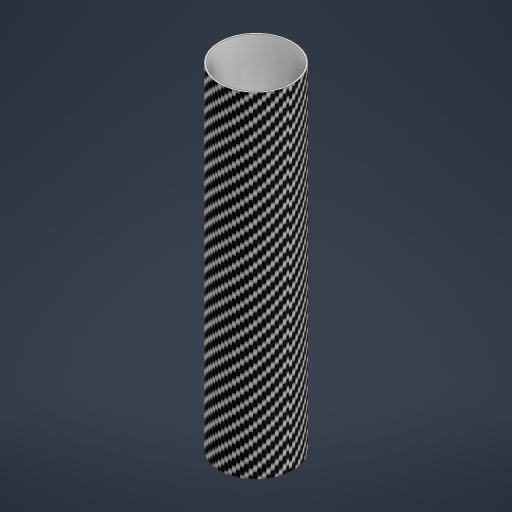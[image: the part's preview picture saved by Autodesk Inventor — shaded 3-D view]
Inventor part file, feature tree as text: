
AUTODESK INVENTOR PART (.ipt)
format: ipt  version: 2023 (Build 270158000, 158)  size: 244,736 bytes
history: native  units: mm
features: extrude x1, sketch x1
ambient origin geometry x8: Origin, YZ Plane, XZ Plane, XY Plane, X Axis, Y Axis, Z Axis, Center Point
bodies: Solid1 (feature_tree)
feature tree (2):
  extrude  "Extrusion1"  Depth=100.0mm
  sketch  "Sketch1"  dims[d0=21.0mm d1=22.0mm d2=100.0mm d3=0.0mm]
